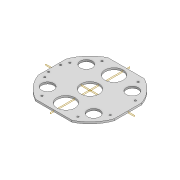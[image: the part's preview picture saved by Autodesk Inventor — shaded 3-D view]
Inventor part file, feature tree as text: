
AUTODESK INVENTOR PART (.ipt)
format: ipt  version: 2022 (Build 260153000, 153)  size: 189,952 bytes
history: native  units: mm
features: extrude x3, plane x2, mirror x2, sketch x2, projected_geometry x1
ambient origin geometry x8: Origin, YZ Plane, XZ Plane, XY Plane, X Axis, Y Axis, Z Axis, Center Point
bodies: Solid1 (feature_tree)
feature tree (10):
  extrude  "Extrusion1"  Depth=3.0mm TaperAngle=0.0deg
  extrude  "Extrusion3"  Depth=10.0mm
  plane  "Work Plane5"
  plane  "Work Plane6"
  mirror  "Mirror3"
  mirror  "Mirror4"
  sketch  "Sketch10"  dims[d0=120.0mm d2=3.0mm d3=0.0mm]
  extrude  "Extrusion6"  Depth=10.0mm TaperAngle=0.0deg
  projected_geometry  "Projected Loop6"
  sketch  "Sketch14"  dims[d25=60.0mm d27=8.726646mm d36=10.0mm d37=0.0mm d38=63.0mm d39=63.0mm d50=3.0mm d51=10.0mm d52=25.0mm d53=40.0mm d54=30.0mm d55=40.0mm d56=20.0mm d57=50.0mm d58=30.0mm d75=3.0mm d76=3.0mm d77=4.0mm d78=4.0mm d79=10.0mm d80=10.0mm d81=10.0mm d82=0.0mm]
